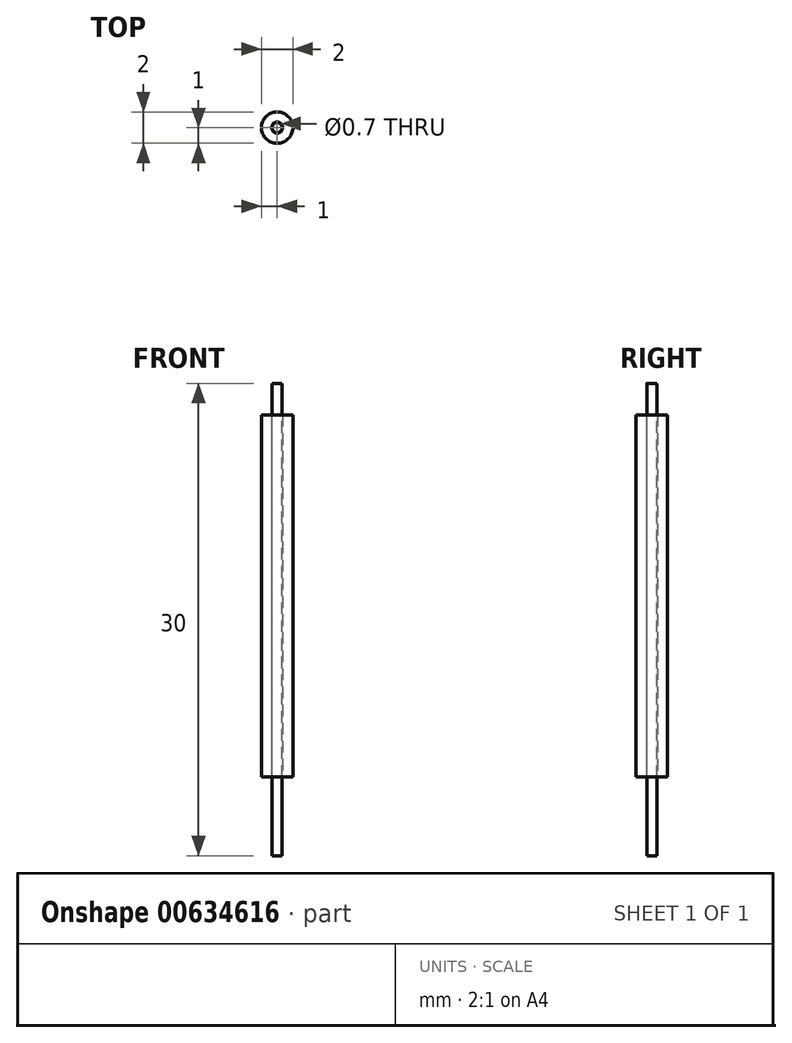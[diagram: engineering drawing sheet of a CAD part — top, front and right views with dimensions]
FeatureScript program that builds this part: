
annotation { "Feature Type Name" : "Feature", "Feature Type Description" : "" }
export const myFeature = defineFeature(function(context is Context, id is Id, definition is map)
    precondition{}
    {
        {
            var Q0;
            Q0=qCreatedBy(makeId("Front.planeOp"),FACE);
            var sketch = newSketch(context, id + "F0", { "sketchPlane" : qUnion([Q0])});
            skLineSegment(sketch, "E0.bottom", {"start": v(0, 0) * mm, "end": v(-0.32, 0) * mm});
            skLineSegment(sketch, "E0.top", {"start": v(0, 0) * mm, "end": v(-0.32, 0) * mm});
            skLineSegment(sketch, "E0.left", {"start": v(0, 0) * mm, "end": v(0, 0) * mm});
            skLineSegment(sketch, "E0.right", {"start": v(-0.32, 0) * mm, "end": v(-0.32, 0) * mm});
            skLineSegment(sketch, "E1.bottom", {"start": v(0, 30) * mm, "end": v(-0.32, 30) * mm});
            skLineSegment(sketch, "E1.left", {"start": v(0, 30) * mm, "end": v(0, 0) * mm});
            skLineSegment(sketch, "E1.right", {"start": v(-0.32, 30) * mm, "end": v(-0.32, 0) * mm});
            skSolve(sketch);
        }
        {
            var Q0;
            Q0 = qSketchRegion(id + "F0", true);
            var Q1;
            Q1=sQuery(id+"F0.wireOp",EDGE,"E1.left");
            revolve(context, id + "F1", {"entities" : qUnion([Q0]), "axis" : qUnion([Q1]), "revolveType" : RevolveType.FULL});
        }
        {
            var Q0;
            Q0=qCreatedBy(makeId("Front.planeOp"),FACE);
            var sketch = newSketch(context, id + "F2", { "sketchPlane" : qUnion([Q0])});
            skLineSegment(sketch, "E2.bottom", {"start": v(-0.35, 5) * mm, "end": v(-1, 5) * mm});
            skLineSegment(sketch, "E2.top", {"start": v(-0.35, 28) * mm, "end": v(-1, 28) * mm});
            skLineSegment(sketch, "E2.left", {"start": v(-0.35, 5) * mm, "end": v(-0.35, 28) * mm});
            skLineSegment(sketch, "E2.right", {"start": v(-1, 5) * mm, "end": v(-1, 28) * mm});
            skLineSegment(sketch, "E3", {"start": v(0, 0) * mm, "end": v(0, 37.8) * mm});
            skSolve(sketch);
        }
        {
            var Q0;
            Q0 = qSketchRegion(id + "F2", true);
            var Q1;
            Q1=sQuery(id+"F2.wireOp",EDGE,"E3");
            revolve(context, id + "F3", {"operationType" : NewBodyOperationType.ADD, "entities" : qUnion([Q0]), "axis" : qUnion([Q1]), "revolveType" : RevolveType.FULL});
        }
    });
